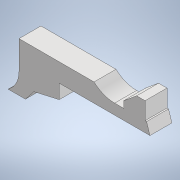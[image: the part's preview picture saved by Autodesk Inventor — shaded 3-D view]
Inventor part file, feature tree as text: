
AUTODESK INVENTOR PART (.ipt)
format: ipt  version: 2022 (Build 260153000, 153)  size: 756,224 bytes
history: native  units: in
note: dims shown in document units (in); Inventor stores cm internally (conversion verified against a paired STEP export)
features: other x5, sheet_metal_op x1, sketch x1, reference x1
ambient origin geometry x8: Origin, YZ Plane, XZ Plane, XY Plane, X Axis, Y Axis, Z Axis, Center Point
bodies: Solid1 (feature_tree)
feature tree (8):
  sheet_metal_op  "Face1"
  sketch  "Sketch1"  dims[d1=3.0666in d2=3.0666in d31=0.12in]
  other  "Image1"
  reference  "Reference1"
  other  "Plate1"
  parser-record x1  (decoder bookkeeping rows leaked as tree rows — omitted from the tree; the rows remain in map.json)
  other  "Assembly1.iam"
  other  "sheetmettaal:2"
note: 1 file-system path scrubbed to <path> (originals preserved in map.json)
